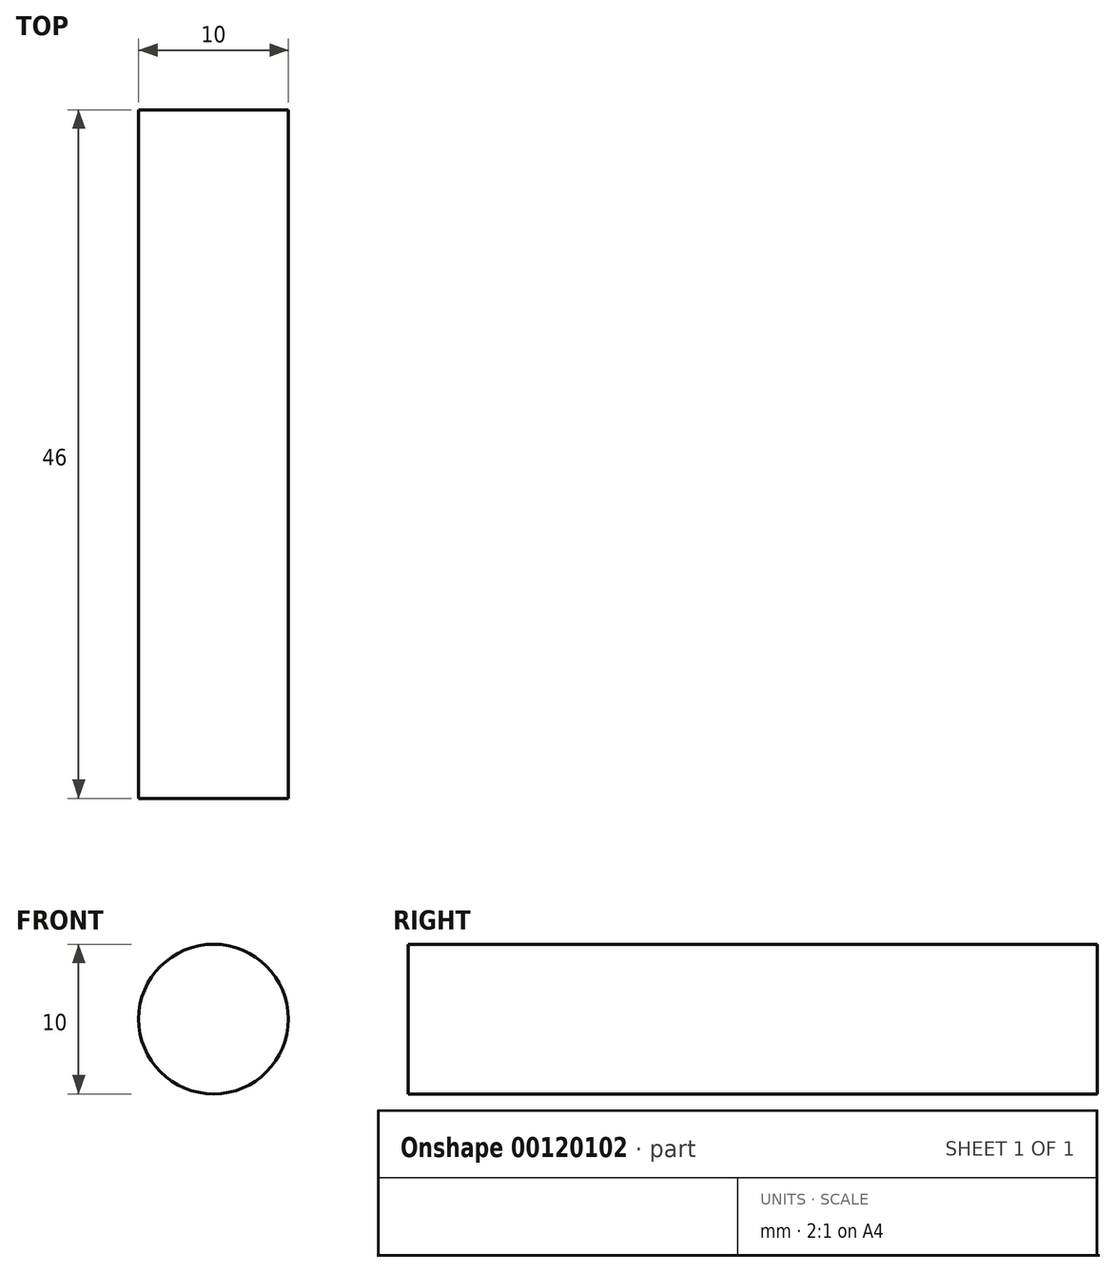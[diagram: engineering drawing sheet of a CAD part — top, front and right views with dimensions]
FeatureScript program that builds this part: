
annotation { "Feature Type Name" : "Feature", "Feature Type Description" : "" }
export const myFeature = defineFeature(function(context is Context, id is Id, definition is map)
    precondition{}
    {
        {
            var Q0;
            Q0=qCreatedBy(makeId("Front.planeOp"),FACE);
            var sketch = newSketch(context, id + "F0", { "sketchPlane" : qUnion([Q0])});
            skCircle(sketch, "E0", {"center": v(0, 0) * mm, "radius": 5 * mm});
            skSolve(sketch);
        }
        {
            var Q0;
            Q0 = qSketchRegion(id + "F0", true);
            extrude(context, id + "F1", {"entities" : qUnion([Q0]), "endBound" : BoundingType.SYMMETRIC, "depth" : 46 * mm});
        }
    });
